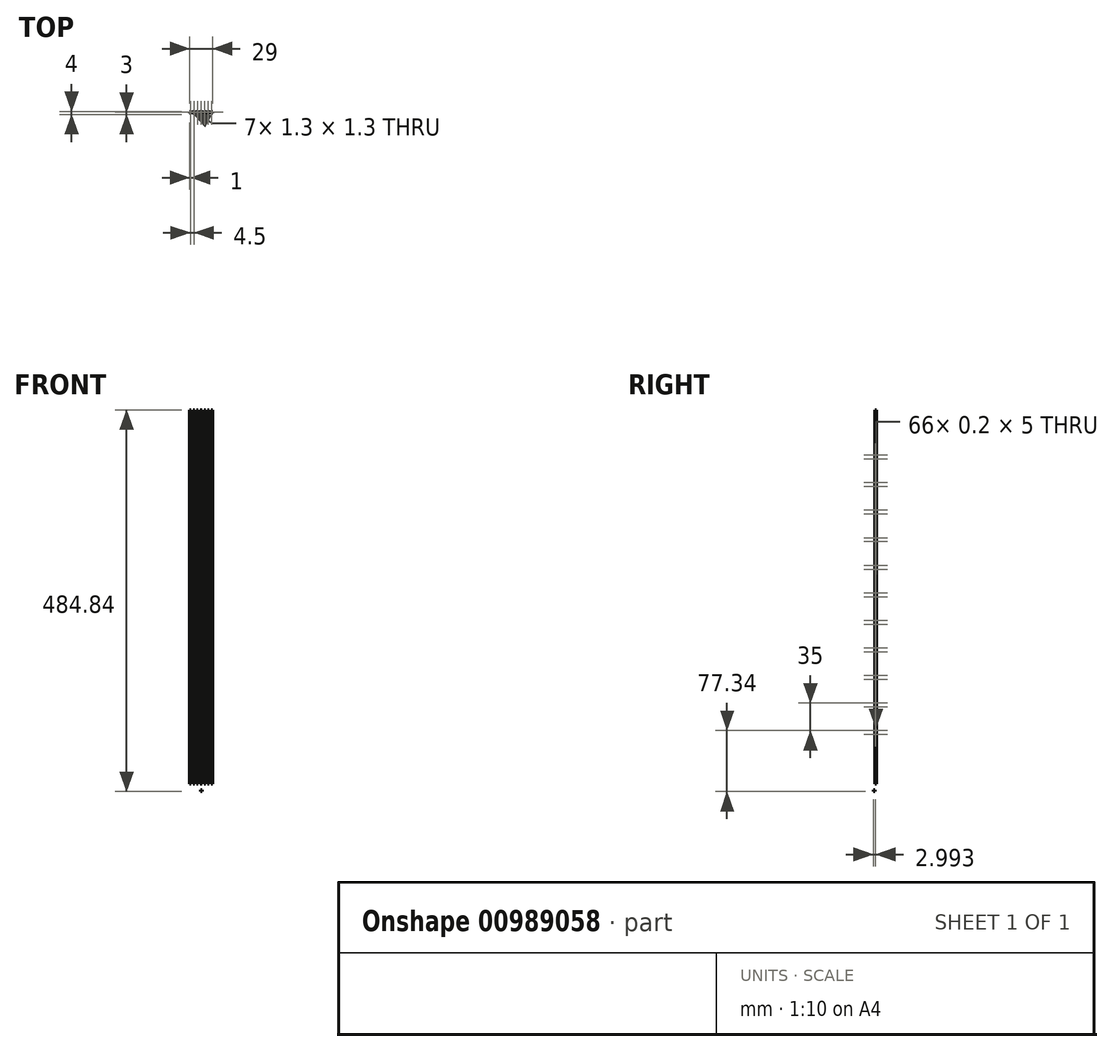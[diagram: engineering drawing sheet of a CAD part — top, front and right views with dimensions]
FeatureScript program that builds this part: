
annotation { "Feature Type Name" : "Feature", "Feature Type Description" : "" }
export const myFeature = defineFeature(function(context is Context, id is Id, definition is map)
    precondition{}
    {
        {
            var Q0;
            Q0=qCreatedBy(makeId("Top.planeOp"),FACE);
            var sketch = newSketch(context, id + "F0", { "sketchPlane" : qUnion([Q0])});
            skLineSegment(sketch, "E0.bottom", {"start": v(0, 0) * mm, "end": v(2, 0) * mm});
            skLineSegment(sketch, "E0.top", {"start": v(0, 2) * mm, "end": v(2, 2) * mm});
            skLineSegment(sketch, "E0.left", {"start": v(0, 0) * mm, "end": v(0, 2) * mm});
            skLineSegment(sketch, "E0.right", {"start": v(2, 0) * mm, "end": v(2, 2) * mm});
            skLineSegment(sketch, "E1.0", {"start": v(1.65, 1.65) * mm, "end": v(1.65, 0.35) * mm});
            skLineSegment(sketch, "E1.1", {"start": v(0.35, 1.65) * mm, "end": v(1.65, 1.65) * mm});
            skLineSegment(sketch, "E1.2", {"start": v(0.35, 1.65) * mm, "end": v(0.35, 0.35) * mm});
            skLineSegment(sketch, "E1.3", {"start": v(0.35, 0.35) * mm, "end": v(1.65, 0.35) * mm});
            skLineSegment(sketch, "E2", {"start": v(2, 1.1) * mm, "end": v(4.5, 1.1) * mm});
            skLineSegment(sketch, "E3", {"start": v(2, 0.9) * mm, "end": v(4.5, 0.9) * mm});
            skLineSegment(sketch, "E4", {"start": v(2, 1.1) * mm, "end": v(2, 0.9) * mm});
            skLineSegment(sketch, "E5.bottom", {"start": v(4.5, 0) * mm, "end": v(6.5, 0) * mm});
            skLineSegment(sketch, "E5.top", {"start": v(4.5, 2) * mm, "end": v(6.5, 2) * mm});
            skLineSegment(sketch, "E5.left", {"start": v(4.5, 0) * mm, "end": v(4.5, 2) * mm});
            skLineSegment(sketch, "E5.right", {"start": v(6.5, 0) * mm, "end": v(6.5, 2) * mm});
            skLineSegment(sketch, "E6.0", {"start": v(6.15, 1.65) * mm, "end": v(6.15, 0.35) * mm});
            skLineSegment(sketch, "E6.1", {"start": v(4.85, 1.65) * mm, "end": v(6.15, 1.65) * mm});
            skLineSegment(sketch, "E6.2", {"start": v(4.85, 1.65) * mm, "end": v(4.85, 0.35) * mm});
            skLineSegment(sketch, "E6.3", {"start": v(4.85, 0.35) * mm, "end": v(6.15, 0.35) * mm});
            skLineSegment(sketch, "E7", {"start": v(6.5, 1.1) * mm, "end": v(9, 1.1) * mm});
            skLineSegment(sketch, "E8", {"start": v(6.5, 0.9) * mm, "end": v(9, 0.9) * mm});
            skLineSegment(sketch, "E9", {"start": v(6.5, 1.1) * mm, "end": v(6.5, 0.9) * mm});
            skLineSegment(sketch, "E10.bottom", {"start": v(9, 0) * mm, "end": v(11, 0) * mm});
            skLineSegment(sketch, "E10.top", {"start": v(9, 2) * mm, "end": v(11, 2) * mm});
            skLineSegment(sketch, "E10.left", {"start": v(9, 0) * mm, "end": v(9, 2) * mm});
            skLineSegment(sketch, "E10.right", {"start": v(11, 0) * mm, "end": v(11, 2) * mm});
            skLineSegment(sketch, "E11.0", {"start": v(10.65, 1.65) * mm, "end": v(10.65, 0.35) * mm});
            skLineSegment(sketch, "E11.1", {"start": v(9.35, 1.65) * mm, "end": v(10.65, 1.65) * mm});
            skLineSegment(sketch, "E11.2", {"start": v(9.35, 1.65) * mm, "end": v(9.35, 0.35) * mm});
            skLineSegment(sketch, "E11.3", {"start": v(9.35, 0.35) * mm, "end": v(10.65, 0.35) * mm});
            skLineSegment(sketch, "E12", {"start": v(11, 1.1) * mm, "end": v(13.5, 1.1) * mm});
            skLineSegment(sketch, "E13", {"start": v(11, 0.9) * mm, "end": v(13.5, 0.9) * mm});
            skLineSegment(sketch, "E14", {"start": v(11, 1.1) * mm, "end": v(11, 0.9) * mm});
            skLineSegment(sketch, "E15.bottom", {"start": v(13.5, 0) * mm, "end": v(15.5, 0) * mm});
            skLineSegment(sketch, "E15.top", {"start": v(13.5, 2) * mm, "end": v(15.5, 2) * mm});
            skLineSegment(sketch, "E15.left", {"start": v(13.5, 0) * mm, "end": v(13.5, 2) * mm});
            skLineSegment(sketch, "E15.right", {"start": v(15.5, 0) * mm, "end": v(15.5, 2) * mm});
            skLineSegment(sketch, "E16.0", {"start": v(15.15, 1.65) * mm, "end": v(15.15, 0.35) * mm});
            skLineSegment(sketch, "E16.1", {"start": v(13.85, 1.65) * mm, "end": v(15.15, 1.65) * mm});
            skLineSegment(sketch, "E16.2", {"start": v(13.85, 1.65) * mm, "end": v(13.85, 0.35) * mm});
            skLineSegment(sketch, "E16.3", {"start": v(13.85, 0.35) * mm, "end": v(15.15, 0.35) * mm});
            skLineSegment(sketch, "E17", {"start": v(15.5, 1.1) * mm, "end": v(18, 1.1) * mm});
            skLineSegment(sketch, "E18", {"start": v(15.5, 0.9) * mm, "end": v(18, 0.9) * mm});
            skLineSegment(sketch, "E19", {"start": v(15.5, 1.1) * mm, "end": v(15.5, 0.9) * mm});
            skLineSegment(sketch, "E20.bottom", {"start": v(18, 0) * mm, "end": v(20, 0) * mm});
            skLineSegment(sketch, "E20.top", {"start": v(18, 2) * mm, "end": v(20, 2) * mm});
            skLineSegment(sketch, "E20.left", {"start": v(18, 0) * mm, "end": v(18, 2) * mm});
            skLineSegment(sketch, "E20.right", {"start": v(20, 0) * mm, "end": v(20, 2) * mm});
            skLineSegment(sketch, "E21.0", {"start": v(19.65, 1.65) * mm, "end": v(19.65, 0.35) * mm});
            skLineSegment(sketch, "E21.1", {"start": v(18.35, 1.65) * mm, "end": v(19.65, 1.65) * mm});
            skLineSegment(sketch, "E21.2", {"start": v(18.35, 1.65) * mm, "end": v(18.35, 0.35) * mm});
            skLineSegment(sketch, "E21.3", {"start": v(18.35, 0.35) * mm, "end": v(19.65, 0.35) * mm});
            skLineSegment(sketch, "E22", {"start": v(20, 1.1) * mm, "end": v(22.5, 1.1) * mm});
            skLineSegment(sketch, "E23", {"start": v(20, 0.9) * mm, "end": v(22.5, 0.9) * mm});
            skLineSegment(sketch, "E24", {"start": v(20, 1.1) * mm, "end": v(20, 0.9) * mm});
            skLineSegment(sketch, "E25.bottom", {"start": v(22.5, 0) * mm, "end": v(24.5, 0) * mm});
            skLineSegment(sketch, "E25.top", {"start": v(22.5, 2) * mm, "end": v(24.5, 2) * mm});
            skLineSegment(sketch, "E25.left", {"start": v(22.5, 0) * mm, "end": v(22.5, 2) * mm});
            skLineSegment(sketch, "E25.right", {"start": v(24.5, 0) * mm, "end": v(24.5, 2) * mm});
            skLineSegment(sketch, "E26.0", {"start": v(24.15, 1.64) * mm, "end": v(24.15, 0.34) * mm});
            skLineSegment(sketch, "E26.1", {"start": v(22.85, 1.64) * mm, "end": v(24.15, 1.64) * mm});
            skLineSegment(sketch, "E26.2", {"start": v(22.85, 1.64) * mm, "end": v(22.85, 0.34) * mm});
            skLineSegment(sketch, "E26.3", {"start": v(22.85, 0.34) * mm, "end": v(24.15, 0.34) * mm});
            skLineSegment(sketch, "E27", {"start": v(24.5, 1.1) * mm, "end": v(27, 1.1) * mm});
            skLineSegment(sketch, "E28", {"start": v(24.5, 0.9) * mm, "end": v(27, 0.9) * mm});
            skLineSegment(sketch, "E29", {"start": v(24.5, 1.1) * mm, "end": v(24.5, 0.9) * mm});
            skLineSegment(sketch, "E30.bottom", {"start": v(27, 0) * mm, "end": v(29, 0) * mm});
            skLineSegment(sketch, "E30.top", {"start": v(27, 2) * mm, "end": v(29, 2) * mm});
            skLineSegment(sketch, "E30.left", {"start": v(27, 0) * mm, "end": v(27, 2) * mm});
            skLineSegment(sketch, "E30.right", {"start": v(29, 0) * mm, "end": v(29, 2) * mm});
            skLineSegment(sketch, "E31.0", {"start": v(28.65, 1.65) * mm, "end": v(28.65, 0.35) * mm});
            skLineSegment(sketch, "E31.1", {"start": v(27.35, 1.65) * mm, "end": v(28.65, 1.65) * mm});
            skLineSegment(sketch, "E31.2", {"start": v(27.35, 1.65) * mm, "end": v(27.35, 0.35) * mm});
            skLineSegment(sketch, "E31.3", {"start": v(27.35, 0.35) * mm, "end": v(28.65, 0.35) * mm});
            skLineSegment(sketch, "E32", {"start": v(29, 1.1) * mm, "end": v(29, 0.9) * mm});
            skSolve(sketch);
        }
        {
            var Q0;
            {var subQ1=sQuery(id+"F0.wireOp",EDGE,"E0.bottom");Q0=makeQuery(id+"F0.imprint","IMPRINT",FACE,{"disambiguationData":[TD([[makeQuery(id+"F0.imprint","IMPRINT",EDGE,{"derivedFrom":subQ1}),1.0]])]});}
            var Q1;
            {var subQ0=sQuery(id+"F0.wireOp",EDGE,"E2");Q1=makeQuery(id+"F0.imprint","IMPRINT",FACE,{"disambiguationData":[TD([[makeQuery(id+"F0.imprint","IMPRINT",EDGE,{"derivedFrom":subQ0}),-1.0]])]});}
            var Q2;
            {var subQ4=sQuery(id+"F0.wireOp",EDGE,"E5.bottom");Q2=makeQuery(id+"F0.imprint","IMPRINT",FACE,{"disambiguationData":[TD([[makeQuery(id+"F0.imprint","IMPRINT",EDGE,{"derivedFrom":subQ4}),1.0]])]});}
            var Q3;
            {var subQ4=sQuery(id+"F0.wireOp",EDGE,"E10.bottom");Q3=makeQuery(id+"F0.imprint","IMPRINT",FACE,{"disambiguationData":[TD([[makeQuery(id+"F0.imprint","IMPRINT",EDGE,{"derivedFrom":subQ4}),1.0]])]});}
            var Q4;
            {var subQ0=sQuery(id+"F0.wireOp",EDGE,"E7");Q4=makeQuery(id+"F0.imprint","IMPRINT",FACE,{"disambiguationData":[TD([[makeQuery(id+"F0.imprint","IMPRINT",EDGE,{"derivedFrom":subQ0}),-1.0]])]});}
            var Q5;
            {var subQ0=sQuery(id+"F0.wireOp",EDGE,"E12");Q5=makeQuery(id+"F0.imprint","IMPRINT",FACE,{"disambiguationData":[TD([[makeQuery(id+"F0.imprint","IMPRINT",EDGE,{"derivedFrom":subQ0}),-1.0]])]});}
            var Q6;
            {var subQ3=sQuery(id+"F0.wireOp",EDGE,"E15.bottom");Q6=makeQuery(id+"F0.imprint","IMPRINT",FACE,{"disambiguationData":[TD([[makeQuery(id+"F0.imprint","IMPRINT",EDGE,{"derivedFrom":subQ3}),1.0]])]});}
            var Q7;
            {var subQ0=sQuery(id+"F0.wireOp",EDGE,"E17");Q7=makeQuery(id+"F0.imprint","IMPRINT",FACE,{"disambiguationData":[TD([[makeQuery(id+"F0.imprint","IMPRINT",EDGE,{"derivedFrom":subQ0}),-1.0]])]});}
            var Q8;
            {var subQ0=sQuery(id+"F0.wireOp",EDGE,"E22");Q8=makeQuery(id+"F0.imprint","IMPRINT",FACE,{"disambiguationData":[TD([[makeQuery(id+"F0.imprint","IMPRINT",EDGE,{"derivedFrom":subQ0}),-1.0]])]});}
            var Q9;
            {var subQ4=sQuery(id+"F0.wireOp",EDGE,"E20.bottom");Q9=makeQuery(id+"F0.imprint","IMPRINT",FACE,{"disambiguationData":[TD([[makeQuery(id+"F0.imprint","IMPRINT",EDGE,{"derivedFrom":subQ4}),1.0]])]});}
            var Q10;
            {var subQ3=sQuery(id+"F0.wireOp",EDGE,"E25.bottom");Q10=makeQuery(id+"F0.imprint","IMPRINT",FACE,{"disambiguationData":[TD([[makeQuery(id+"F0.imprint","IMPRINT",EDGE,{"derivedFrom":subQ3}),1.0]])]});}
            var Q11;
            {var subQ1=sQuery(id+"F0.wireOp",EDGE,"E30.bottom");Q11=makeQuery(id+"F0.imprint","IMPRINT",FACE,{"disambiguationData":[TD([[makeQuery(id+"F0.imprint","IMPRINT",EDGE,{"derivedFrom":subQ1}),1.0]])]});}
            var Q12;
            {var subQ0=sQuery(id+"F0.wireOp",EDGE,"E27");Q12=makeQuery(id+"F0.imprint","IMPRINT",FACE,{"disambiguationData":[TD([[makeQuery(id+"F0.imprint","IMPRINT",EDGE,{"derivedFrom":subQ0}),-1.0]])]});}
            extrude(context, id + "F1", {"entities" : qUnion([Q0, Q1, Q2, Q3, Q4, Q5, Q6, Q7, Q8, Q9, Q10, Q11, Q12]), "depth" : 475 * mm, "offsetDistance" : 25 * mm});
        }
        {
            var Q0;
            Q0=makeQuery(id+"F1.opExtrude","SWEPT_FACE",FACE,{"disambiguationData":[OSD([sQuery(id+"F0.wireOp",EDGE,"E3")])]});
            var sketch = newSketch(context, id + "F2", { "sketchPlane" : qUnion([Q0])});
            skLineSegment(sketch, "E33", {"start": v(2, 60) * mm, "end": v(4.5, 60) * mm});
            skLineSegment(sketch, "E34.bottom", {"start": v(4.5, 60) * mm, "end": v(2, 60) * mm});
            skLineSegment(sketch, "E34.top", {"start": v(4.5, 65) * mm, "end": v(2, 65) * mm});
            skLineSegment(sketch, "E34.left", {"start": v(4.5, 60) * mm, "end": v(4.5, 65) * mm});
            skLineSegment(sketch, "E34.right", {"start": v(2, 60) * mm, "end": v(2, 65) * mm});
            skLineSegment(sketch, "E35", {"start": v(2, 95) * mm, "end": v(4.5, 95) * mm});
            skLineSegment(sketch, "E36", {"start": v(2, 100) * mm, "end": v(4.5, 100) * mm});
            skLineSegment(sketch, "E37", {"start": v(2, 130) * mm, "end": v(4.5, 130) * mm});
            skLineSegment(sketch, "E38", {"start": v(2, 135) * mm, "end": v(4.5, 135) * mm});
            skLineSegment(sketch, "E39", {"start": v(2, 165) * mm, "end": v(4.5, 165) * mm});
            skLineSegment(sketch, "E40", {"start": v(2, 170) * mm, "end": v(4.5, 170) * mm});
            skLineSegment(sketch, "E41", {"start": v(2, 200) * mm, "end": v(4.5, 200) * mm});
            skLineSegment(sketch, "E42", {"start": v(2, 205) * mm, "end": v(4.5, 205) * mm});
            skLineSegment(sketch, "E43", {"start": v(2, 235) * mm, "end": v(4.5, 235) * mm});
            skLineSegment(sketch, "E44", {"start": v(2, 240) * mm, "end": v(4.5, 240) * mm});
            skPoint(sketch, "E44.endSnap0", {"position": v(4.5, 237.5) * mm});
            skLineSegment(sketch, "E45", {"start": v(2, 270) * mm, "end": v(4.5, 270) * mm});
            skLineSegment(sketch, "E46", {"start": v(2, 275) * mm, "end": v(4.5, 275) * mm});
            skLineSegment(sketch, "E47", {"start": v(2, 305) * mm, "end": v(4.5, 305) * mm});
            skLineSegment(sketch, "E48", {"start": v(2, 310) * mm, "end": v(4.5, 310) * mm});
            skLineSegment(sketch, "E49", {"start": v(2, 340) * mm, "end": v(4.5, 340) * mm});
            skLineSegment(sketch, "E50", {"start": v(2, 345) * mm, "end": v(4.5, 345) * mm});
            skLineSegment(sketch, "E51", {"start": v(2, 375) * mm, "end": v(4.5, 375) * mm});
            skLineSegment(sketch, "E52", {"start": v(2, 380) * mm, "end": v(4.5, 380) * mm});
            skLineSegment(sketch, "E53", {"start": v(2, 410) * mm, "end": v(4.5, 410) * mm});
            skLineSegment(sketch, "E54", {"start": v(2, 415) * mm, "end": v(4.5, 415) * mm});
            skSolve(sketch);
        }
        {
            var Q0;
            {var subQ0=sQuery(id+"F2.wireOp",EDGE,"E33");Q0=makeQuery(id+"F2.imprint","IMPRINT",FACE,{"disambiguationData":[TD([[makeQuery(id+"F2.imprint","IMPRINT",EDGE,{"derivedFrom":subQ0}),-1.0]])]});}
            var Q1;
            {var subQ0=sQuery(id+"F2.wireOp",EDGE,"E34.top");Q1=makeQuery(id+"F2.imprint","IMPRINT",FACE,{"disambiguationData":[TD([[makeQuery(id+"F2.imprint","IMPRINT",EDGE,{"derivedFrom":subQ0}),-1.0]])]});}
            var Q2;
            {var subQ0=sQuery(id+"F2.wireOp",EDGE,"E36");Q2=makeQuery(id+"F2.imprint","IMPRINT",FACE,{"disambiguationData":[TD([[makeQuery(id+"F2.imprint","IMPRINT",EDGE,{"derivedFrom":subQ0}),1.0]])]});}
            var Q3;
            {var subQ0=sQuery(id+"F2.wireOp",EDGE,"E38");Q3=makeQuery(id+"F2.imprint","IMPRINT",FACE,{"disambiguationData":[TD([[makeQuery(id+"F2.imprint","IMPRINT",EDGE,{"derivedFrom":subQ0}),1.0]])]});}
            var Q4;
            {var subQ0=sQuery(id+"F2.wireOp",EDGE,"E40");Q4=makeQuery(id+"F2.imprint","IMPRINT",FACE,{"disambiguationData":[TD([[makeQuery(id+"F2.imprint","IMPRINT",EDGE,{"derivedFrom":subQ0}),1.0]])]});}
            var Q5;
            {var subQ0=sQuery(id+"F2.wireOp",EDGE,"E42");Q5=makeQuery(id+"F2.imprint","IMPRINT",FACE,{"disambiguationData":[TD([[makeQuery(id+"F2.imprint","IMPRINT",EDGE,{"derivedFrom":subQ0}),1.0]])]});}
            var Q6;
            {var subQ0=sQuery(id+"F2.wireOp",EDGE,"E44");Q6=makeQuery(id+"F2.imprint","IMPRINT",FACE,{"disambiguationData":[TD([[makeQuery(id+"F2.imprint","IMPRINT",EDGE,{"derivedFrom":subQ0}),1.0]])]});}
            var Q7;
            {var subQ0=sQuery(id+"F2.wireOp",EDGE,"E46");Q7=makeQuery(id+"F2.imprint","IMPRINT",FACE,{"disambiguationData":[TD([[makeQuery(id+"F2.imprint","IMPRINT",EDGE,{"derivedFrom":subQ0}),1.0]])]});}
            var Q8;
            {var subQ0=sQuery(id+"F2.wireOp",EDGE,"E48");Q8=makeQuery(id+"F2.imprint","IMPRINT",FACE,{"disambiguationData":[TD([[makeQuery(id+"F2.imprint","IMPRINT",EDGE,{"derivedFrom":subQ0}),1.0]])]});}
            var Q9;
            {var subQ0=sQuery(id+"F2.wireOp",EDGE,"E50");Q9=makeQuery(id+"F2.imprint","IMPRINT",FACE,{"disambiguationData":[TD([[makeQuery(id+"F2.imprint","IMPRINT",EDGE,{"derivedFrom":subQ0}),1.0]])]});}
            var Q10;
            {var subQ0=sQuery(id+"F2.wireOp",EDGE,"E52");Q10=makeQuery(id+"F2.imprint","IMPRINT",FACE,{"disambiguationData":[TD([[makeQuery(id+"F2.imprint","IMPRINT",EDGE,{"derivedFrom":subQ0}),1.0]])]});}
            var Q11;
            {var subQ0=sQuery(id+"F2.wireOp",EDGE,"E54");Q11=makeQuery(id+"F2.imprint","IMPRINT",FACE,{"disambiguationData":[TD([[makeQuery(id+"F2.imprint","IMPRINT",EDGE,{"derivedFrom":subQ0}),1.0]])]});}
            extrude(context, id + "F3", {"entities" : qUnion([Q0, Q1, Q2, Q3, Q4, Q5, Q6, Q7, Q8, Q9, Q10, Q11]), "operationType" : NewBodyOperationType.REMOVE, "oppositeDirection" : true, "depth" : 4.8 * mm, "offsetDistance" : 25 * mm});
        }
        {
            var Q0;
            Q0=makeQuery(id+"F1.opExtrude","SWEPT_FACE",FACE,{"disambiguationData":[OSD([sQuery(id+"F0.wireOp",EDGE,"E8")])]});
            var sketch = newSketch(context, id + "F4", { "sketchPlane" : qUnion([Q0])});
            skLineSegment(sketch, "E55", {"start": v(6.5, 65) * mm, "end": v(9, 65) * mm});
            skLineSegment(sketch, "E56", {"start": v(6.5, 70) * mm, "end": v(9, 70) * mm});
            skLineSegment(sketch, "E57", {"start": v(6.5, 100) * mm, "end": v(9, 100) * mm});
            skLineSegment(sketch, "E58", {"start": v(6.5, 105) * mm, "end": v(9, 105) * mm});
            skLineSegment(sketch, "E59", {"start": v(6.5, 135) * mm, "end": v(9, 135) * mm});
            skLineSegment(sketch, "E60", {"start": v(6.5, 140) * mm, "end": v(9, 140) * mm});
            skLineSegment(sketch, "E61", {"start": v(6.5, 170) * mm, "end": v(9, 170) * mm});
            skLineSegment(sketch, "E62", {"start": v(6.5, 175) * mm, "end": v(9, 175) * mm});
            skLineSegment(sketch, "E63", {"start": v(6.5, 205) * mm, "end": v(9, 205) * mm});
            skLineSegment(sketch, "E64", {"start": v(6.5, 210) * mm, "end": v(9, 210) * mm});
            skLineSegment(sketch, "E65", {"start": v(6.5, 240) * mm, "end": v(9, 240) * mm});
            skLineSegment(sketch, "E66", {"start": v(6.5, 245) * mm, "end": v(9, 245) * mm});
            skLineSegment(sketch, "E67", {"start": v(6.5, 275) * mm, "end": v(9, 275) * mm});
            skLineSegment(sketch, "E68", {"start": v(6.5, 280) * mm, "end": v(9, 280) * mm});
            skLineSegment(sketch, "E69", {"start": v(6.5, 310) * mm, "end": v(9, 310) * mm});
            skLineSegment(sketch, "E70", {"start": v(6.5, 315) * mm, "end": v(9, 315) * mm});
            skLineSegment(sketch, "E71", {"start": v(6.5, 345) * mm, "end": v(9, 345) * mm});
            skLineSegment(sketch, "E72", {"start": v(6.5, 350) * mm, "end": v(9, 350) * mm});
            skLineSegment(sketch, "E73", {"start": v(6.5, 380) * mm, "end": v(9, 380) * mm});
            skLineSegment(sketch, "E74", {"start": v(6.5, 385) * mm, "end": v(9, 385) * mm});
            skLineSegment(sketch, "E75", {"start": v(6.5, 415) * mm, "end": v(9, 415) * mm});
            skLineSegment(sketch, "E76", {"start": v(6.5, 420) * mm, "end": v(9, 420) * mm});
            skSolve(sketch);
        }
        {
            var Q0;
            {var subQ0=sQuery(id+"F4.wireOp",EDGE,"E55");Q0=makeQuery(id+"F4.imprint","IMPRINT",FACE,{"disambiguationData":[TD([[makeQuery(id+"F4.imprint","IMPRINT",EDGE,{"derivedFrom":subQ0}),-1.0]])]});}
            var Q1;
            {var subQ0=sQuery(id+"F4.wireOp",EDGE,"E56");Q1=makeQuery(id+"F4.imprint","IMPRINT",FACE,{"disambiguationData":[TD([[makeQuery(id+"F4.imprint","IMPRINT",EDGE,{"derivedFrom":subQ0}),1.0]])]});}
            var Q2;
            {var subQ0=sQuery(id+"F4.wireOp",EDGE,"E58");Q2=makeQuery(id+"F4.imprint","IMPRINT",FACE,{"disambiguationData":[TD([[makeQuery(id+"F4.imprint","IMPRINT",EDGE,{"derivedFrom":subQ0}),1.0]])]});}
            var Q3;
            {var subQ0=sQuery(id+"F4.wireOp",EDGE,"E60");Q3=makeQuery(id+"F4.imprint","IMPRINT",FACE,{"disambiguationData":[TD([[makeQuery(id+"F4.imprint","IMPRINT",EDGE,{"derivedFrom":subQ0}),1.0]])]});}
            var Q4;
            {var subQ0=sQuery(id+"F4.wireOp",EDGE,"E62");Q4=makeQuery(id+"F4.imprint","IMPRINT",FACE,{"disambiguationData":[TD([[makeQuery(id+"F4.imprint","IMPRINT",EDGE,{"derivedFrom":subQ0}),1.0]])]});}
            var Q5;
            {var subQ0=sQuery(id+"F4.wireOp",EDGE,"E64");Q5=makeQuery(id+"F4.imprint","IMPRINT",FACE,{"disambiguationData":[TD([[makeQuery(id+"F4.imprint","IMPRINT",EDGE,{"derivedFrom":subQ0}),1.0]])]});}
            var Q6;
            {var subQ0=sQuery(id+"F4.wireOp",EDGE,"E66");Q6=makeQuery(id+"F4.imprint","IMPRINT",FACE,{"disambiguationData":[TD([[makeQuery(id+"F4.imprint","IMPRINT",EDGE,{"derivedFrom":subQ0}),1.0]])]});}
            var Q7;
            {var subQ0=sQuery(id+"F4.wireOp",EDGE,"E68");Q7=makeQuery(id+"F4.imprint","IMPRINT",FACE,{"disambiguationData":[TD([[makeQuery(id+"F4.imprint","IMPRINT",EDGE,{"derivedFrom":subQ0}),1.0]])]});}
            var Q8;
            {var subQ0=sQuery(id+"F4.wireOp",EDGE,"E70");Q8=makeQuery(id+"F4.imprint","IMPRINT",FACE,{"disambiguationData":[TD([[makeQuery(id+"F4.imprint","IMPRINT",EDGE,{"derivedFrom":subQ0}),1.0]])]});}
            var Q9;
            {var subQ0=sQuery(id+"F4.wireOp",EDGE,"E72");Q9=makeQuery(id+"F4.imprint","IMPRINT",FACE,{"disambiguationData":[TD([[makeQuery(id+"F4.imprint","IMPRINT",EDGE,{"derivedFrom":subQ0}),1.0]])]});}
            var Q10;
            {var subQ0=sQuery(id+"F4.wireOp",EDGE,"E74");Q10=makeQuery(id+"F4.imprint","IMPRINT",FACE,{"disambiguationData":[TD([[makeQuery(id+"F4.imprint","IMPRINT",EDGE,{"derivedFrom":subQ0}),1.0]])]});}
            var Q11;
            {var subQ0=sQuery(id+"F4.wireOp",EDGE,"E76");Q11=makeQuery(id+"F4.imprint","IMPRINT",FACE,{"disambiguationData":[TD([[makeQuery(id+"F4.imprint","IMPRINT",EDGE,{"derivedFrom":subQ0}),1.0]])]});}
            extrude(context, id + "F5", {"entities" : qUnion([Q0, Q1, Q2, Q3, Q4, Q5, Q6, Q7, Q8, Q9, Q10, Q11]), "operationType" : NewBodyOperationType.REMOVE, "endBound" : BoundingType.THROUGH_ALL, "oppositeDirection" : true, "depth" : 19.1 * mm, "offsetDistance" : 25 * mm});
        }
        {
            var Q0;
            Q0=makeQuery(id+"F1.opExtrude","SWEPT_FACE",FACE,{"disambiguationData":[OSD([sQuery(id+"F0.wireOp",EDGE,"E13")])]});
            var sketch = newSketch(context, id + "F6", { "sketchPlane" : qUnion([Q0])});
            skLineSegment(sketch, "E77", {"start": v(11, 60) * mm, "end": v(13.5, 60) * mm});
            skLineSegment(sketch, "E78", {"start": v(11, 65) * mm, "end": v(13.5, 65) * mm});
            skLineSegment(sketch, "E79", {"start": v(11, 95) * mm, "end": v(13.5, 95) * mm});
            skLineSegment(sketch, "E80", {"start": v(11, 100) * mm, "end": v(13.5, 100) * mm});
            skLineSegment(sketch, "E81", {"start": v(11, 130) * mm, "end": v(13.5, 130) * mm});
            skLineSegment(sketch, "E82", {"start": v(11, 135) * mm, "end": v(13.5, 135) * mm});
            skLineSegment(sketch, "E83", {"start": v(11, 165) * mm, "end": v(13.5, 165) * mm});
            skLineSegment(sketch, "E84", {"start": v(11, 170) * mm, "end": v(13.5, 170) * mm});
            skLineSegment(sketch, "E85", {"start": v(11, 200) * mm, "end": v(13.5, 200) * mm});
            skLineSegment(sketch, "E86", {"start": v(11, 205) * mm, "end": v(13.5, 205) * mm});
            skLineSegment(sketch, "E87", {"start": v(11, 235) * mm, "end": v(13.5, 235) * mm});
            skLineSegment(sketch, "E88", {"start": v(11, 240) * mm, "end": v(13.5, 240) * mm});
            skLineSegment(sketch, "E89", {"start": v(11, 270) * mm, "end": v(13.5, 270) * mm});
            skLineSegment(sketch, "E90", {"start": v(11, 275) * mm, "end": v(13.5, 275) * mm});
            skLineSegment(sketch, "E91", {"start": v(11, 305) * mm, "end": v(13.5, 305) * mm});
            skLineSegment(sketch, "E92", {"start": v(11, 310) * mm, "end": v(13.5, 310) * mm});
            skLineSegment(sketch, "E93", {"start": v(11, 340) * mm, "end": v(13.5, 340) * mm});
            skLineSegment(sketch, "E94", {"start": v(11, 345) * mm, "end": v(13.5, 345) * mm});
            skLineSegment(sketch, "E95", {"start": v(11, 375) * mm, "end": v(13.5, 375) * mm});
            skLineSegment(sketch, "E96", {"start": v(11, 380) * mm, "end": v(13.5, 380) * mm});
            skLineSegment(sketch, "E97", {"start": v(11, 410) * mm, "end": v(13.5, 410) * mm});
            skLineSegment(sketch, "E98", {"start": v(11, 415) * mm, "end": v(13.5, 415) * mm});
            skSolve(sketch);
        }
        {
            var Q0;
            Q0 = qSketchRegion(id + "F6", true);
            var Q1;
            {var subQ0=sQuery(id+"F6.wireOp",EDGE,"E77");Q1=makeQuery(id+"F6.imprint","IMPRINT",FACE,{"disambiguationData":[TD([[makeQuery(id+"F6.imprint","IMPRINT",EDGE,{"derivedFrom":subQ0}),-1.0]])]});}
            var Q2;
            {var subQ0=sQuery(id+"F6.wireOp",EDGE,"E78");Q2=makeQuery(id+"F6.imprint","IMPRINT",FACE,{"disambiguationData":[TD([[makeQuery(id+"F6.imprint","IMPRINT",EDGE,{"derivedFrom":subQ0}),1.0]])]});}
            var Q3;
            {var subQ0=sQuery(id+"F6.wireOp",EDGE,"E80");Q3=makeQuery(id+"F6.imprint","IMPRINT",FACE,{"disambiguationData":[TD([[makeQuery(id+"F6.imprint","IMPRINT",EDGE,{"derivedFrom":subQ0}),1.0]])]});}
            var Q4;
            {var subQ0=sQuery(id+"F6.wireOp",EDGE,"E82");Q4=makeQuery(id+"F6.imprint","IMPRINT",FACE,{"disambiguationData":[TD([[makeQuery(id+"F6.imprint","IMPRINT",EDGE,{"derivedFrom":subQ0}),1.0]])]});}
            var Q5;
            {var subQ0=sQuery(id+"F6.wireOp",EDGE,"E84");Q5=makeQuery(id+"F6.imprint","IMPRINT",FACE,{"disambiguationData":[TD([[makeQuery(id+"F6.imprint","IMPRINT",EDGE,{"derivedFrom":subQ0}),1.0]])]});}
            var Q6;
            {var subQ0=sQuery(id+"F6.wireOp",EDGE,"E86");Q6=makeQuery(id+"F6.imprint","IMPRINT",FACE,{"disambiguationData":[TD([[makeQuery(id+"F6.imprint","IMPRINT",EDGE,{"derivedFrom":subQ0}),1.0]])]});}
            var Q7;
            {var subQ0=sQuery(id+"F6.wireOp",EDGE,"E88");Q7=makeQuery(id+"F6.imprint","IMPRINT",FACE,{"disambiguationData":[TD([[makeQuery(id+"F6.imprint","IMPRINT",EDGE,{"derivedFrom":subQ0}),1.0]])]});}
            var Q8;
            {var subQ0=sQuery(id+"F6.wireOp",EDGE,"E90");Q8=makeQuery(id+"F6.imprint","IMPRINT",FACE,{"disambiguationData":[TD([[makeQuery(id+"F6.imprint","IMPRINT",EDGE,{"derivedFrom":subQ0}),1.0]])]});}
            var Q9;
            {var subQ0=sQuery(id+"F6.wireOp",EDGE,"E92");Q9=makeQuery(id+"F6.imprint","IMPRINT",FACE,{"disambiguationData":[TD([[makeQuery(id+"F6.imprint","IMPRINT",EDGE,{"derivedFrom":subQ0}),1.0]])]});}
            var Q10;
            {var subQ0=sQuery(id+"F6.wireOp",EDGE,"E94");Q10=makeQuery(id+"F6.imprint","IMPRINT",FACE,{"disambiguationData":[TD([[makeQuery(id+"F6.imprint","IMPRINT",EDGE,{"derivedFrom":subQ0}),1.0]])]});}
            var Q11;
            {var subQ0=sQuery(id+"F6.wireOp",EDGE,"E96");Q11=makeQuery(id+"F6.imprint","IMPRINT",FACE,{"disambiguationData":[TD([[makeQuery(id+"F6.imprint","IMPRINT",EDGE,{"derivedFrom":subQ0}),1.0]])]});}
            var Q12;
            {var subQ0=sQuery(id+"F6.wireOp",EDGE,"E98");Q12=makeQuery(id+"F6.imprint","IMPRINT",FACE,{"disambiguationData":[TD([[makeQuery(id+"F6.imprint","IMPRINT",EDGE,{"derivedFrom":subQ0}),1.0]])]});}
            extrude(context, id + "F7", {"entities" : qUnion([Q0, Q1, Q2, Q3, Q4, Q5, Q6, Q7, Q8, Q9, Q10, Q11, Q12]), "operationType" : NewBodyOperationType.REMOVE, "endBound" : BoundingType.THROUGH_ALL, "oppositeDirection" : true, "depth" : 25 * mm, "offsetDistance" : 25 * mm});
        }
        {
            var Q0;
            Q0=makeQuery(id+"F1.opExtrude","SWEPT_FACE",FACE,{"disambiguationData":[OSD([sQuery(id+"F0.wireOp",EDGE,"E18")])]});
            var sketch = newSketch(context, id + "F8", { "sketchPlane" : qUnion([Q0])});
            skLineSegment(sketch, "E99", {"start": v(15.5, 65) * mm, "end": v(18, 65) * mm});
            skLineSegment(sketch, "E100", {"start": v(15.5, 70) * mm, "end": v(18, 70) * mm});
            skLineSegment(sketch, "E101", {"start": v(15.5, 100) * mm, "end": v(18, 100) * mm});
            skLineSegment(sketch, "E102", {"start": v(15.5, 105) * mm, "end": v(18, 105) * mm});
            skLineSegment(sketch, "E103", {"start": v(15.5, 135) * mm, "end": v(18, 135) * mm});
            skLineSegment(sketch, "E104", {"start": v(15.5, 140) * mm, "end": v(18, 140) * mm});
            skLineSegment(sketch, "E105", {"start": v(15.5, 170) * mm, "end": v(18, 170) * mm});
            skLineSegment(sketch, "E106", {"start": v(15.5, 175) * mm, "end": v(18, 175) * mm});
            skLineSegment(sketch, "E107", {"start": v(15.5, 205) * mm, "end": v(18, 205) * mm});
            skLineSegment(sketch, "E108", {"start": v(15.5, 210) * mm, "end": v(18, 210) * mm});
            skLineSegment(sketch, "E109", {"start": v(15.5, 240) * mm, "end": v(18, 240) * mm});
            skLineSegment(sketch, "E110", {"start": v(15.5, 275) * mm, "end": v(18, 275) * mm});
            skLineSegment(sketch, "E111", {"start": v(15.5, 280) * mm, "end": v(18, 280) * mm});
            skLineSegment(sketch, "E112", {"start": v(15.5, 245) * mm, "end": v(18, 245) * mm});
            skLineSegment(sketch, "E113", {"start": v(15.5, 310) * mm, "end": v(18, 310) * mm});
            skLineSegment(sketch, "E114", {"start": v(15.5, 315) * mm, "end": v(18, 315) * mm});
            skLineSegment(sketch, "E115", {"start": v(15.5, 345) * mm, "end": v(18, 345) * mm});
            skLineSegment(sketch, "E116", {"start": v(15.5, 350) * mm, "end": v(18, 350) * mm});
            skLineSegment(sketch, "E117", {"start": v(15.5, 380) * mm, "end": v(18, 380) * mm});
            skLineSegment(sketch, "E118", {"start": v(15.5, 385) * mm, "end": v(18, 385) * mm});
            skLineSegment(sketch, "E119", {"start": v(15.5, 415) * mm, "end": v(18, 415) * mm});
            skLineSegment(sketch, "E120", {"start": v(15.5, 420) * mm, "end": v(18, 420) * mm});
            skSolve(sketch);
        }
        {
            var Q0;
            Q0 = qSketchRegion(id + "F8", true);
            var Q1;
            {var subQ0=sQuery(id+"F8.wireOp",EDGE,"E120");Q1=makeQuery(id+"F8.imprint","IMPRINT",FACE,{"disambiguationData":[TD([[makeQuery(id+"F8.imprint","IMPRINT",EDGE,{"derivedFrom":subQ0}),1.0]])]});}
            var Q2;
            {var subQ0=sQuery(id+"F8.wireOp",EDGE,"E118");Q2=makeQuery(id+"F8.imprint","IMPRINT",FACE,{"disambiguationData":[TD([[makeQuery(id+"F8.imprint","IMPRINT",EDGE,{"derivedFrom":subQ0}),1.0]])]});}
            var Q3;
            {var subQ0=sQuery(id+"F8.wireOp",EDGE,"E116");Q3=makeQuery(id+"F8.imprint","IMPRINT",FACE,{"disambiguationData":[TD([[makeQuery(id+"F8.imprint","IMPRINT",EDGE,{"derivedFrom":subQ0}),1.0]])]});}
            var Q4;
            {var subQ0=sQuery(id+"F8.wireOp",EDGE,"E114");Q4=makeQuery(id+"F8.imprint","IMPRINT",FACE,{"disambiguationData":[TD([[makeQuery(id+"F8.imprint","IMPRINT",EDGE,{"derivedFrom":subQ0}),1.0]])]});}
            var Q5;
            {var subQ0=sQuery(id+"F8.wireOp",EDGE,"E111");Q5=makeQuery(id+"F8.imprint","IMPRINT",FACE,{"disambiguationData":[TD([[makeQuery(id+"F8.imprint","IMPRINT",EDGE,{"derivedFrom":subQ0}),1.0]])]});}
            var Q6;
            {var subQ0=sQuery(id+"F8.wireOp",EDGE,"E110");Q6=makeQuery(id+"F8.imprint","IMPRINT",FACE,{"disambiguationData":[TD([[makeQuery(id+"F8.imprint","IMPRINT",EDGE,{"derivedFrom":subQ0}),-1.0]])]});}
            var Q7;
            {var subQ0=sQuery(id+"F8.wireOp",EDGE,"E108");Q7=makeQuery(id+"F8.imprint","IMPRINT",FACE,{"disambiguationData":[TD([[makeQuery(id+"F8.imprint","IMPRINT",EDGE,{"derivedFrom":subQ0}),1.0]])]});}
            var Q8;
            {var subQ0=sQuery(id+"F8.wireOp",EDGE,"E106");Q8=makeQuery(id+"F8.imprint","IMPRINT",FACE,{"disambiguationData":[TD([[makeQuery(id+"F8.imprint","IMPRINT",EDGE,{"derivedFrom":subQ0}),1.0]])]});}
            var Q9;
            {var subQ0=sQuery(id+"F8.wireOp",EDGE,"E104");Q9=makeQuery(id+"F8.imprint","IMPRINT",FACE,{"disambiguationData":[TD([[makeQuery(id+"F8.imprint","IMPRINT",EDGE,{"derivedFrom":subQ0}),1.0]])]});}
            var Q10;
            {var subQ0=sQuery(id+"F8.wireOp",EDGE,"E102");Q10=makeQuery(id+"F8.imprint","IMPRINT",FACE,{"disambiguationData":[TD([[makeQuery(id+"F8.imprint","IMPRINT",EDGE,{"derivedFrom":subQ0}),1.0]])]});}
            var Q11;
            {var subQ0=sQuery(id+"F8.wireOp",EDGE,"E100");Q11=makeQuery(id+"F8.imprint","IMPRINT",FACE,{"disambiguationData":[TD([[makeQuery(id+"F8.imprint","IMPRINT",EDGE,{"derivedFrom":subQ0}),1.0]])]});}
            var Q12;
            {var subQ0=sQuery(id+"F8.wireOp",EDGE,"E99");Q12=makeQuery(id+"F8.imprint","IMPRINT",FACE,{"disambiguationData":[TD([[makeQuery(id+"F8.imprint","IMPRINT",EDGE,{"derivedFrom":subQ0}),-1.0]])]});}
            extrude(context, id + "F9", {"entities" : qUnion([Q0, Q1, Q2, Q3, Q4, Q5, Q6, Q7, Q8, Q9, Q10, Q11, Q12]), "operationType" : NewBodyOperationType.REMOVE, "endBound" : BoundingType.THROUGH_ALL, "oppositeDirection" : true, "depth" : 25 * mm, "offsetDistance" : 25 * mm});
        }
        {
            var Q0;
            Q0=makeQuery(id+"F1.opExtrude","SWEPT_FACE",FACE,{"disambiguationData":[OSD([sQuery(id+"F0.wireOp",EDGE,"E23")])]});
            var sketch = newSketch(context, id + "F10", { "sketchPlane" : qUnion([Q0])});
            skLineSegment(sketch, "E121", {"start": v(20, 60) * mm, "end": v(22.5, 60) * mm});
            skLineSegment(sketch, "E122", {"start": v(20, 65) * mm, "end": v(22.5, 65) * mm});
            skLineSegment(sketch, "E123", {"start": v(20, 95) * mm, "end": v(22.5, 95) * mm});
            skLineSegment(sketch, "E124", {"start": v(20, 100) * mm, "end": v(22.5, 100) * mm});
            skLineSegment(sketch, "E125", {"start": v(20, 130) * mm, "end": v(22.5, 130) * mm});
            skLineSegment(sketch, "E126", {"start": v(20, 135) * mm, "end": v(22.5, 135) * mm});
            skLineSegment(sketch, "E127", {"start": v(20, 165) * mm, "end": v(22.5, 165) * mm});
            skLineSegment(sketch, "E128", {"start": v(20, 170) * mm, "end": v(22.5, 170) * mm});
            skLineSegment(sketch, "E129", {"start": v(20, 200) * mm, "end": v(22.5, 200) * mm});
            skLineSegment(sketch, "E130", {"start": v(20, 205) * mm, "end": v(22.5, 205) * mm});
            skLineSegment(sketch, "E131", {"start": v(20, 235) * mm, "end": v(22.5, 235) * mm});
            skLineSegment(sketch, "E132", {"start": v(20, 240) * mm, "end": v(22.5, 240) * mm});
            skLineSegment(sketch, "E133", {"start": v(20, 270) * mm, "end": v(22.5, 270) * mm});
            skLineSegment(sketch, "E134", {"start": v(20, 275) * mm, "end": v(22.5, 275) * mm});
            skLineSegment(sketch, "E135", {"start": v(20, 305) * mm, "end": v(22.5, 305) * mm});
            skLineSegment(sketch, "E136", {"start": v(20, 310) * mm, "end": v(22.5, 310) * mm});
            skLineSegment(sketch, "E137", {"start": v(20, 340) * mm, "end": v(22.5, 340) * mm});
            skLineSegment(sketch, "E138", {"start": v(20, 345) * mm, "end": v(22.5, 345) * mm});
            skLineSegment(sketch, "E139", {"start": v(20, 375) * mm, "end": v(22.5, 375) * mm});
            skLineSegment(sketch, "E140", {"start": v(20, 380) * mm, "end": v(22.5, 380) * mm});
            skLineSegment(sketch, "E141", {"start": v(20, 410) * mm, "end": v(22.5, 410) * mm});
            skLineSegment(sketch, "E142", {"start": v(20, 415) * mm, "end": v(22.5, 415) * mm});
            skSolve(sketch);
        }
        {
            var Q0;
            Q0 = qSketchRegion(id + "F10", true);
            var Q1;
            {var subQ0=sQuery(id+"F10.wireOp",EDGE,"E142");Q1=makeQuery(id+"F10.imprint","IMPRINT",FACE,{"disambiguationData":[TD([[makeQuery(id+"F10.imprint","IMPRINT",EDGE,{"derivedFrom":subQ0}),1.0]])]});}
            var Q2;
            {var subQ0=sQuery(id+"F10.wireOp",EDGE,"E140");Q2=makeQuery(id+"F10.imprint","IMPRINT",FACE,{"disambiguationData":[TD([[makeQuery(id+"F10.imprint","IMPRINT",EDGE,{"derivedFrom":subQ0}),1.0]])]});}
            var Q3;
            {var subQ0=sQuery(id+"F10.wireOp",EDGE,"E138");Q3=makeQuery(id+"F10.imprint","IMPRINT",FACE,{"disambiguationData":[TD([[makeQuery(id+"F10.imprint","IMPRINT",EDGE,{"derivedFrom":subQ0}),1.0]])]});}
            var Q4;
            {var subQ0=sQuery(id+"F10.wireOp",EDGE,"E136");Q4=makeQuery(id+"F10.imprint","IMPRINT",FACE,{"disambiguationData":[TD([[makeQuery(id+"F10.imprint","IMPRINT",EDGE,{"derivedFrom":subQ0}),1.0]])]});}
            var Q5;
            {var subQ0=sQuery(id+"F10.wireOp",EDGE,"E134");Q5=makeQuery(id+"F10.imprint","IMPRINT",FACE,{"disambiguationData":[TD([[makeQuery(id+"F10.imprint","IMPRINT",EDGE,{"derivedFrom":subQ0}),1.0]])]});}
            var Q6;
            {var subQ0=sQuery(id+"F10.wireOp",EDGE,"E132");Q6=makeQuery(id+"F10.imprint","IMPRINT",FACE,{"disambiguationData":[TD([[makeQuery(id+"F10.imprint","IMPRINT",EDGE,{"derivedFrom":subQ0}),1.0]])]});}
            var Q7;
            {var subQ0=sQuery(id+"F10.wireOp",EDGE,"E130");Q7=makeQuery(id+"F10.imprint","IMPRINT",FACE,{"disambiguationData":[TD([[makeQuery(id+"F10.imprint","IMPRINT",EDGE,{"derivedFrom":subQ0}),1.0]])]});}
            var Q8;
            {var subQ0=sQuery(id+"F10.wireOp",EDGE,"E128");Q8=makeQuery(id+"F10.imprint","IMPRINT",FACE,{"disambiguationData":[TD([[makeQuery(id+"F10.imprint","IMPRINT",EDGE,{"derivedFrom":subQ0}),1.0]])]});}
            var Q9;
            {var subQ0=sQuery(id+"F10.wireOp",EDGE,"E126");Q9=makeQuery(id+"F10.imprint","IMPRINT",FACE,{"disambiguationData":[TD([[makeQuery(id+"F10.imprint","IMPRINT",EDGE,{"derivedFrom":subQ0}),1.0]])]});}
            var Q10;
            {var subQ0=sQuery(id+"F10.wireOp",EDGE,"E124");Q10=makeQuery(id+"F10.imprint","IMPRINT",FACE,{"disambiguationData":[TD([[makeQuery(id+"F10.imprint","IMPRINT",EDGE,{"derivedFrom":subQ0}),1.0]])]});}
            var Q11;
            {var subQ0=sQuery(id+"F10.wireOp",EDGE,"E122");Q11=makeQuery(id+"F10.imprint","IMPRINT",FACE,{"disambiguationData":[TD([[makeQuery(id+"F10.imprint","IMPRINT",EDGE,{"derivedFrom":subQ0}),1.0]])]});}
            var Q12;
            {var subQ0=sQuery(id+"F10.wireOp",EDGE,"E121");Q12=makeQuery(id+"F10.imprint","IMPRINT",FACE,{"disambiguationData":[TD([[makeQuery(id+"F10.imprint","IMPRINT",EDGE,{"derivedFrom":subQ0}),-1.0]])]});}
            extrude(context, id + "F11", {"entities" : qUnion([Q0, Q1, Q2, Q3, Q4, Q5, Q6, Q7, Q8, Q9, Q10, Q11, Q12]), "operationType" : NewBodyOperationType.REMOVE, "endBound" : BoundingType.THROUGH_ALL, "oppositeDirection" : true, "depth" : 25 * mm, "offsetDistance" : 25 * mm});
        }
        {
            var Q0;
            Q0=makeQuery(id+"F1.opExtrude","SWEPT_FACE",FACE,{"disambiguationData":[OSD([sQuery(id+"F0.wireOp",EDGE,"E28")])]});
            var sketch = newSketch(context, id + "F12", { "sketchPlane" : qUnion([Q0])});
            skLineSegment(sketch, "E143", {"start": v(24.5, 65) * mm, "end": v(27, 65) * mm});
            skLineSegment(sketch, "E144", {"start": v(24.5, 70) * mm, "end": v(27, 70) * mm});
            skLineSegment(sketch, "E145", {"start": v(24.5, 100) * mm, "end": v(27, 100) * mm});
            skLineSegment(sketch, "E146", {"start": v(24.5, 105) * mm, "end": v(27, 105) * mm});
            skLineSegment(sketch, "E147", {"start": v(24.5, 135) * mm, "end": v(27, 135) * mm});
            skLineSegment(sketch, "E148", {"start": v(24.5, 140) * mm, "end": v(27, 140) * mm});
            skLineSegment(sketch, "E149", {"start": v(24.5, 170) * mm, "end": v(27, 170) * mm});
            skLineSegment(sketch, "E150", {"start": v(24.5, 175) * mm, "end": v(27, 175) * mm});
            skLineSegment(sketch, "E151", {"start": v(24.5, 205) * mm, "end": v(27, 205) * mm});
            skLineSegment(sketch, "E152", {"start": v(24.5, 210) * mm, "end": v(27, 210) * mm});
            skLineSegment(sketch, "E153", {"start": v(24.5, 240) * mm, "end": v(27, 240) * mm});
            skLineSegment(sketch, "E154", {"start": v(24.5, 245) * mm, "end": v(27, 245) * mm});
            skLineSegment(sketch, "E155", {"start": v(24.5, 275) * mm, "end": v(27, 275) * mm});
            skLineSegment(sketch, "E156", {"start": v(24.5, 280) * mm, "end": v(27, 280) * mm});
            skLineSegment(sketch, "E157", {"start": v(24.5, 310) * mm, "end": v(27, 310) * mm});
            skLineSegment(sketch, "E158", {"start": v(24.5, 315) * mm, "end": v(27, 315) * mm});
            skLineSegment(sketch, "E159", {"start": v(24.5, 345) * mm, "end": v(27, 345) * mm});
            skLineSegment(sketch, "E160", {"start": v(24.5, 350) * mm, "end": v(27, 350) * mm});
            skLineSegment(sketch, "E161", {"start": v(24.5, 380) * mm, "end": v(27, 380) * mm});
            skLineSegment(sketch, "E162", {"start": v(24.5, 385) * mm, "end": v(27, 385) * mm});
            skLineSegment(sketch, "E163", {"start": v(24.5, 415) * mm, "end": v(27, 415) * mm});
            skLineSegment(sketch, "E164", {"start": v(24.5, 420) * mm, "end": v(27, 420) * mm});
            skSolve(sketch);
        }
        {
            var Q0;
            Q0 = qSketchRegion(id + "F12", true);
            var Q1;
            {var subQ0=sQuery(id+"F12.wireOp",EDGE,"E164");Q1=makeQuery(id+"F12.imprint","IMPRINT",FACE,{"disambiguationData":[TD([[makeQuery(id+"F12.imprint","IMPRINT",EDGE,{"derivedFrom":subQ0}),1.0]])]});}
            var Q2;
            {var subQ0=sQuery(id+"F12.wireOp",EDGE,"E162");Q2=makeQuery(id+"F12.imprint","IMPRINT",FACE,{"disambiguationData":[TD([[makeQuery(id+"F12.imprint","IMPRINT",EDGE,{"derivedFrom":subQ0}),1.0]])]});}
            var Q3;
            {var subQ0=sQuery(id+"F12.wireOp",EDGE,"E160");Q3=makeQuery(id+"F12.imprint","IMPRINT",FACE,{"disambiguationData":[TD([[makeQuery(id+"F12.imprint","IMPRINT",EDGE,{"derivedFrom":subQ0}),1.0]])]});}
            var Q4;
            {var subQ0=sQuery(id+"F12.wireOp",EDGE,"E158");Q4=makeQuery(id+"F12.imprint","IMPRINT",FACE,{"disambiguationData":[TD([[makeQuery(id+"F12.imprint","IMPRINT",EDGE,{"derivedFrom":subQ0}),1.0]])]});}
            var Q5;
            {var subQ0=sQuery(id+"F12.wireOp",EDGE,"E156");Q5=makeQuery(id+"F12.imprint","IMPRINT",FACE,{"disambiguationData":[TD([[makeQuery(id+"F12.imprint","IMPRINT",EDGE,{"derivedFrom":subQ0}),1.0]])]});}
            var Q6;
            {var subQ0=sQuery(id+"F12.wireOp",EDGE,"E154");Q6=makeQuery(id+"F12.imprint","IMPRINT",FACE,{"disambiguationData":[TD([[makeQuery(id+"F12.imprint","IMPRINT",EDGE,{"derivedFrom":subQ0}),1.0]])]});}
            var Q7;
            {var subQ0=sQuery(id+"F12.wireOp",EDGE,"E152");Q7=makeQuery(id+"F12.imprint","IMPRINT",FACE,{"disambiguationData":[TD([[makeQuery(id+"F12.imprint","IMPRINT",EDGE,{"derivedFrom":subQ0}),1.0]])]});}
            var Q8;
            {var subQ0=sQuery(id+"F12.wireOp",EDGE,"E150");Q8=makeQuery(id+"F12.imprint","IMPRINT",FACE,{"disambiguationData":[TD([[makeQuery(id+"F12.imprint","IMPRINT",EDGE,{"derivedFrom":subQ0}),1.0]])]});}
            var Q9;
            {var subQ0=sQuery(id+"F12.wireOp",EDGE,"E148");Q9=makeQuery(id+"F12.imprint","IMPRINT",FACE,{"disambiguationData":[TD([[makeQuery(id+"F12.imprint","IMPRINT",EDGE,{"derivedFrom":subQ0}),1.0]])]});}
            var Q10;
            {var subQ0=sQuery(id+"F12.wireOp",EDGE,"E146");Q10=makeQuery(id+"F12.imprint","IMPRINT",FACE,{"disambiguationData":[TD([[makeQuery(id+"F12.imprint","IMPRINT",EDGE,{"derivedFrom":subQ0}),1.0]])]});}
            var Q11;
            {var subQ0=sQuery(id+"F12.wireOp",EDGE,"E144");Q11=makeQuery(id+"F12.imprint","IMPRINT",FACE,{"disambiguationData":[TD([[makeQuery(id+"F12.imprint","IMPRINT",EDGE,{"derivedFrom":subQ0}),1.0]])]});}
            var Q12;
            {var subQ0=sQuery(id+"F12.wireOp",EDGE,"E143");Q12=makeQuery(id+"F12.imprint","IMPRINT",FACE,{"disambiguationData":[TD([[makeQuery(id+"F12.imprint","IMPRINT",EDGE,{"derivedFrom":subQ0}),-1.0]])]});}
            extrude(context, id + "F13", {"entities" : qUnion([Q0, Q1, Q2, Q3, Q4, Q5, Q6, Q7, Q8, Q9, Q10, Q11, Q12]), "operationType" : NewBodyOperationType.REMOVE, "endBound" : BoundingType.THROUGH_ALL, "oppositeDirection" : true, "depth" : 25 * mm, "offsetDistance" : 25 * mm});
        }
        {
            var Q0;
            Q0=qCreatedBy(makeId("Front.planeOp"),FACE);
            var sketch = newSketch(context, id + "F14", { "sketchPlane" : qUnion([Q0])});
            skLineSegment(sketch, "E165.bottom", {"start": v(13.95, -7.84) * mm, "end": v(15.95, -7.84) * mm});
            skLineSegment(sketch, "E165.top", {"start": v(13.95, -9.84) * mm, "end": v(15.95, -9.84) * mm});
            skLineSegment(sketch, "E165.left", {"start": v(13.95, -7.84) * mm, "end": v(13.95, -9.84) * mm});
            skLineSegment(sketch, "E165.right", {"start": v(15.95, -7.84) * mm, "end": v(15.95, -9.84) * mm});
            skSolve(sketch);
        }
        {
            var Q0;
            Q0=makeQuery(id+"F14.imprint","IMPRINT",FACE,{"disambiguationData":[TD([[makeQuery(id+"F14.imprint","IMPRINT",EDGE,{"derivedFrom":sQuery(id+"F14.wireOp",EDGE,"E165.bottom")}),-1.0]])]});
            extrude(context, id + "F15", {"entities" : qUnion([Q0]), "depth" : 2 * mm, "offsetDistance" : 25 * mm});
        }
    });
